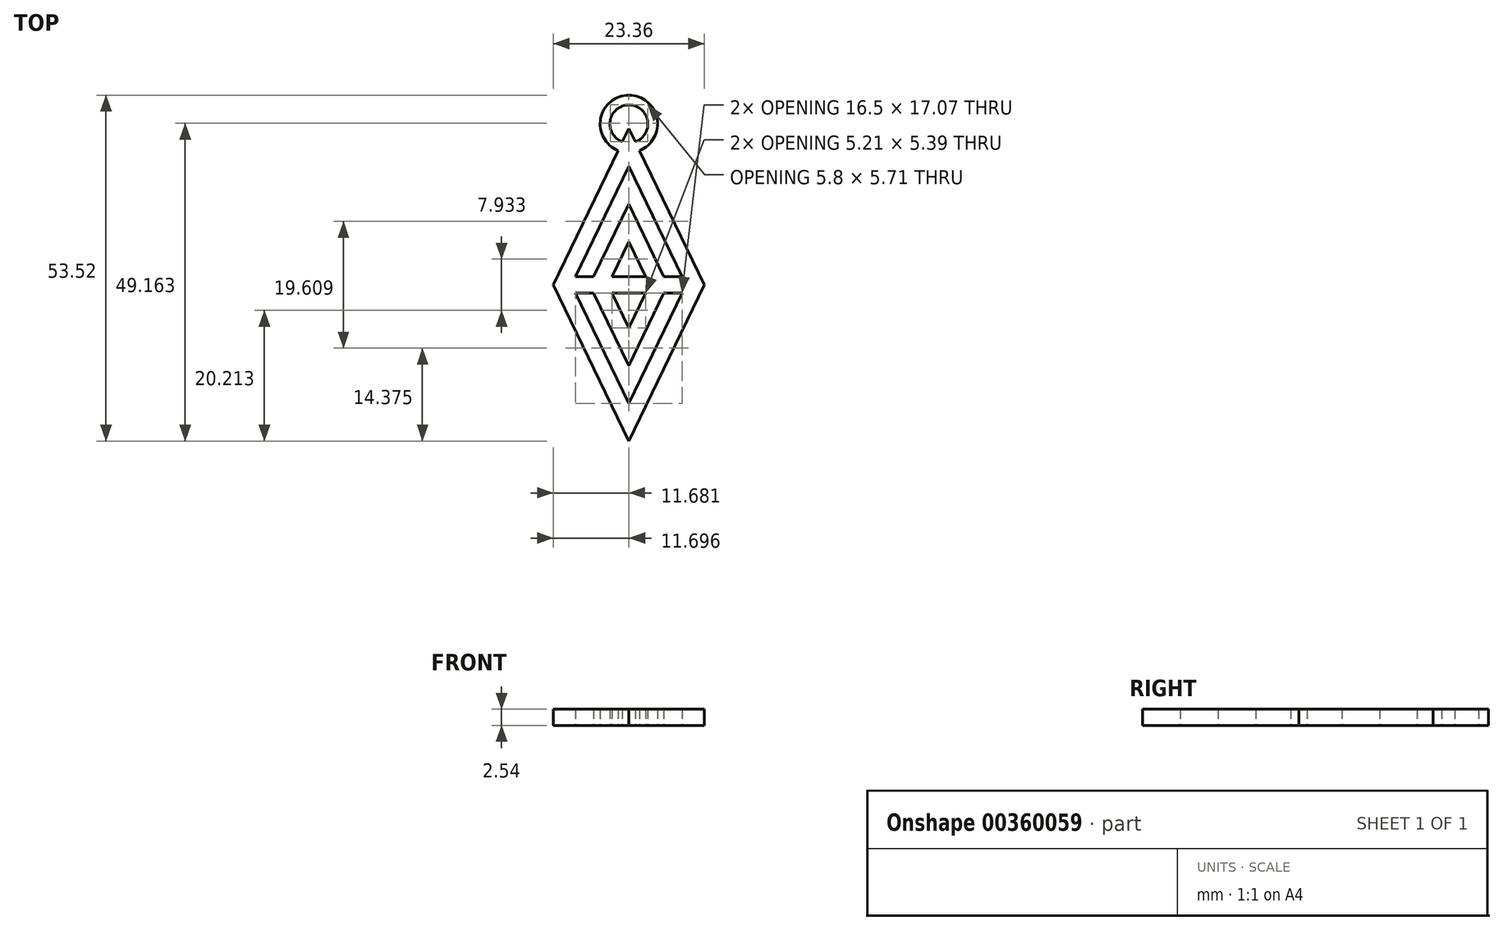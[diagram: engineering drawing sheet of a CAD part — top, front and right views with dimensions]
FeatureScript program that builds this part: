
annotation { "Feature Type Name" : "Feature", "Feature Type Description" : "" }
export const myFeature = defineFeature(function(context is Context, id is Id, definition is map)
    precondition{}
    {
        {
            var Q0;
            Q0=qCreatedBy(makeId("Top.planeOp"),FACE);
            var sketch = newSketch(context, id + "F0", { "sketchPlane" : qUnion([Q0])});
            skPoint(sketch, "E0.middle", {"position": v(0, 0) * mm});
            skLineSegment(sketch, "E1", {"start": v(0, 24.18) * mm, "end": v(-0.99, 22.13) * mm});
            skLineSegment(sketch, "E2", {"start": v(-11.68, 0) * mm, "end": v(0, -24.18) * mm});
            skPoint(sketch, "E3.orphan", {"position": v(0, -10.61) * mm});
            skPoint(sketch, "E4.orphan", {"position": v(0, -15.68) * mm});
            skPoint(sketch, "E5.orphan", {"position": v(0, -20.81) * mm});
            skArc(sketch, "E6", {"start": v(1, 22.13) * mm, "mid": v(0.03, 27.84) * mm, "end": v(-0.99, 22.13) * mm});
            skPoint(sketch, "E6.first.point", {"position": v(-0.99, 22.13) * mm});
            skPoint(sketch, "E6.second.point", {"position": v(0.93, 27.7) * mm});
            skPoint(sketch, "E6.third.point", {"position": v(2.86, 24.18) * mm});
            skArc(sketch, "E7.trimOffspring", {"start": v(1.65, 20.77) * mm, "mid": v(0.03, 29.34) * mm, "end": v(-1.64, 20.78) * mm});
            skPoint(sketch, "E0.left.start.orphan", {"position": v(19.44, 24.18) * mm});
            skPoint(sketch, "E0.right.start.orphan", {"position": v(-19.44, 24.18) * mm});
            skPoint(sketch, "E8.orphan", {"position": v(19.44, -24.18) * mm});
            skPoint(sketch, "E0.top.end.orphan", {"position": v(-19.44, -24.18) * mm});
            skPoint(sketch, "E9.orphan", {"position": v(3.73, 0) * mm});
            skPoint(sketch, "E10.orphan", {"position": v(-3.67, 0) * mm});
            skPoint(sketch, "E11.orphan", {"position": v(-9.21, 0) * mm});
            skPoint(sketch, "E12.orphan", {"position": v(-6.11, 0) * mm});
            skPoint(sketch, "E13.orphan", {"position": v(5.63, 0) * mm});
            skPoint(sketch, "E14.orphan", {"position": v(8.06, 0) * mm});
            skLineSegment(sketch, "E15.trimOffspring", {"start": v(-1.64, 20.78) * mm, "end": v(-11.68, 0) * mm});
            skPoint(sketch, "E16.start.orphan", {"position": v(0, 13.72) * mm});
            skPoint(sketch, "E17.start.orphan", {"position": v(0, 9.13) * mm});
            skPoint(sketch, "E18.start.orphan", {"position": v(-5.4, 1.6) * mm});
            skPoint(sketch, "E19.start.orphan", {"position": v(-3.03, 1.6) * mm});
            skPoint(sketch, "E20.start.orphan", {"position": v(-3.19, -1.4) * mm});
            skPoint(sketch, "E21.start.orphan", {"position": v(-5.57, -1.4) * mm});
            skPoint(sketch, "E22.end.orphan", {"position": v(3.24, -1.4) * mm});
            skPoint(sketch, "E23.start.orphan", {"position": v(4.97, 1.6) * mm});
            skPoint(sketch, "E24.end.orphan", {"position": v(5.13, -1.4) * mm});
            skLineSegment(sketch, "E25", {"start": v(11.68, 0) * mm, "end": v(1.65, 20.77) * mm});
            skLineSegment(sketch, "E26", {"start": v(11.68, 0) * mm, "end": v(0, -24.18) * mm});
            skPoint(sketch, "E27.end.orphan", {"position": v(10.7, 0) * mm});
            skLineSegment(sketch, "E28.trimOffspring", {"start": v(1, 22.13) * mm, "end": v(0, 24.18) * mm});
            skLineSegment(sketch, "E29.0", {"start": v(0, 18.34) * mm, "end": v(-8.25, 1.27) * mm});
            skLineSegment(sketch, "E30.0", {"start": v(8.25, 1.27) * mm, "end": v(0, 18.34) * mm});
            skLineSegment(sketch, "E31.0", {"start": v(-8.25, -1.27) * mm, "end": v(0, -18.34) * mm});
            skLineSegment(sketch, "E32.0", {"start": v(8.25, -1.27) * mm, "end": v(0, -18.34) * mm});
            skLineSegment(sketch, "E33.0", {"start": v(5.43, 1.27) * mm, "end": v(0, 12.5) * mm});
            skLineSegment(sketch, "E34.0", {"start": v(-5.43, -1.27) * mm, "end": v(0, -12.5) * mm});
            skLineSegment(sketch, "E35.0", {"start": v(5.43, -1.27) * mm, "end": v(0, -12.5) * mm});
            skLineSegment(sketch, "E36.trimOffspring", {"start": v(0, 12.5) * mm, "end": v(-5.43, 1.27) * mm});
            skLineSegment(sketch, "E37.0", {"start": v(0, 6.66) * mm, "end": v(-2.6, 1.27) * mm});
            skLineSegment(sketch, "E38.0", {"start": v(2.6, 1.27) * mm, "end": v(0, 6.66) * mm});
            skLineSegment(sketch, "E39.0", {"start": v(-2.6, -1.27) * mm, "end": v(0, -6.66) * mm});
            skLineSegment(sketch, "E40.0", {"start": v(2.6, -1.27) * mm, "end": v(0, -6.66) * mm});
            skLineSegment(sketch, "E41.0", {"start": v(-8.25, -1.27) * mm, "end": v(-5.43, -1.27) * mm});
            skLineSegment(sketch, "E42.trimOffspring", {"start": v(-8.25, 1.27) * mm, "end": v(-5.43, 1.27) * mm});
            skLineSegment(sketch, "E43.trimOffspring", {"start": v(-2.6, 1.27) * mm, "end": v(2.6, 1.27) * mm});
            skLineSegment(sketch, "E44.trimOffspring", {"start": v(-2.6, -1.27) * mm, "end": v(2.6, -1.27) * mm});
            skLineSegment(sketch, "E45.trimOffspring", {"start": v(5.43, 1.27) * mm, "end": v(8.25, 1.27) * mm});
            skLineSegment(sketch, "E46.trimOffspring", {"start": v(5.43, -1.27) * mm, "end": v(8.25, -1.27) * mm});
            skSolve(sketch);
        }
        {
            var Q0;
            Q0=makeQuery(id+"F0.imprint","IMPRINT",FACE,{"disambiguationData":[TD([[makeQuery(id+"F0.imprint","IMPRINT",EDGE,{"derivedFrom":sQuery(id+"F0.wireOp",EDGE,"E1")}),1.0]])]});
            extrude(context, id + "F1", {"entities" : qUnion([Q0]), "depth" : 2.54 * mm, "offsetDistance" : 25.4 * mm});
        }
    });
